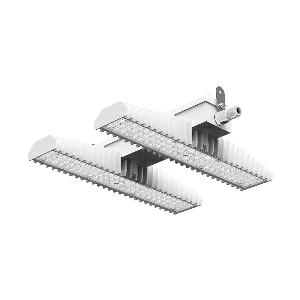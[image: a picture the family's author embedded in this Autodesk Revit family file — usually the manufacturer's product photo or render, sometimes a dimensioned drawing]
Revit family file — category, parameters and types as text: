
# Revit family: 3f_filippi_-_3f_lem_medio_3f_filippi_-_58911_-_3f_lem_2_led_100_dali_cr_medio
name_source: partatom
category: Lighting Fixtures
units: mm (PartAtom-declared; Revit-internal decimal feet)

## family parameters
Cut with Voids When Loaded = No
Host = Face
Light Source = No
Part Type = Normal
Room Calculation Point = No
Round Connector Dimension = Use Diameter
Shared = No

## types (1)
- 3F Filippi - 3F LEM Medio (1 x LED, 16630 lm, 109 W, 4000 K)
    Apparent Load = 109 VA
    Approval mark = CE
    CIE Flux Codes = 83 96 99 100 100
    Color Rendering = 80
    Color Temperature = 4000 K
    Control Gear = Electronic transformer
    Default Elevation = 1800 mm
    Description = Industrial luminaire with high light output and high luminous efficiency designed with the most innovative technologies for environments with temperature up to 55°C.

ILLUMINOTECHNICAL
Luminous efficiency 100% (DLOR 100%, ULOR 0%).
Initial luminous flux of the luminaire 16630 lm.
Medium distribution with rectangular shape.
Installation Interdistance Transv.D = 1.17 x hu - Long.D = 1.21 x hu.
Tabular UGR (CIE 117 - 4H-8H; S=0.25H; 70/50/20): RUG 18.5 - 18.1.
Beam angle: 65° - 67°.
Luminous efficacy 153 lm/W.
Lifetime (L93/B10): 30000 h. (tq+25°C)
Lifetime (L90/B10): 50000 h. (tq+25°C)
Lifetime (L85/B10): 80000 h. (tq+25°C)
Lifetime (L80/B10): 100000 h. (tq+25°C)
Lifetime (L85/B10): 50000 h. (tq+55°C)
Sudden decreased luminous flux after 50000 hours: 0% (C0).
Photobiological safety in compliance with IEC/TR 62778: RG0 risk exempt, (IEC 62471).
In compliance with IEC/EN 62722-2-1 - IEC/EN 62717 standards.

SOURCE
2 Mid-Power linear LED modules 50W/840.
Energy efficiency class (UE 2019/2020 - UE 2019/2015): C.
CIE 13.3 Colour rendering index: CRI >80 (R9 <50%).
IES TM-30 Fidelity Index: Rf = 84 Rg = 95.
CCT nominal colour temperature 4000 K.
Colour initial tolerance (MacAdam): SDCM 3.

MECHANICAL
Passive modular heatsinks in die-casted aluminium, painted in white colour.
To optimize the thermal management of the LED module, the heatsinks are oversized and provided with self-cleaning of cooling fins.
Wiring body in aluminium and galvanised steel anchored solidly to the sinks and thermally separated.
3F Lens lenses with high luminous efficiency, transparent methacrylate (PMMA), fixed to the LED modules.
Fixing brackets in stainless steel.
Luminaire with limited surface temperature. - D - (EN 60598-2-24)
Dimensions: 470x542 mm, height 129 mm. Weight 9.16 kg.
IP65 protection degree.
Mechanical strength to impacts IK06 (1 joule).
Glow-wire test resistance 650°C.

ELECTRICAL
Halogen Free DALI-2 DATI (Parts 251, 252, 253), PUSH-DIM, electronic wiring 230V-50/60Hz, power factor 0.97 at full load, THD <25%, constant output current, class I, 1 driver, 1 DALI addresse.
Power of the luminaire 109 W.
ENEC - CE.
Flicker: <4%.
Luminaire compliant with EN 60598-2-22 for power supply from a centralised emergency system CPSS (Central Power Supply System), not incorporated in the luminaire - high risk areas excluded. The default power and flux are 100% in AC and 15% in DC.
Ambient temperature from -30°C to +55°C.
Temperature class T6 max 85°C.
Quick connection via M25 5P connector with 9-13 mm tightening range.
Power unit positioned on a separate compartment by the LED module to ensure optimum temperatures of cabling components, to be inspectable and maintainable.
Relative humidity UR: <85%.

INSTALLATION
Ceiling / Suspended / Wall.
All accessories dedicated to this product are available on the Catalog and on our website www.3F-Filippi.com.

APPLICATIONS
In commercial environments, exhibition and industrial areas, stores, open areas.
Applications with high ambient temperature up to 55°C.
Environments in which it is necessary a total protection against falling fragments (eg environments with foodstuffs or machines with moving parts or with extreme temperature changes), use luminaires with polycarbonate lenses.

LIGHT MANAGEMENT
Recommended minimum setting: 10%.
The luminaire, equipped with (DALI-2 DATI) driver, can be controlled manually with 3F Easy Dim technology or automatically/manually with wired or wireless DALI/D2D control systems.
The D2D driver guarantees interoperability with other devices with the same certification by making the following information available:
Device Data (Part 251), Energy Report (Part 252), Diagnosis & Maintenance (Part 253).
In electrical systems without a regulation system (manual or automatic) and DALI bus, a suitable jumper must be made on the DA-DA terminals of the appliance.

WARNING
Fixture not suitable for cold stores with an ambient temperature <0°C and/or relative humidity >85%.
Luminaire designed for disposal/recycling at end-of-life.
Replaceable (LED only) light source by a professional. Replaceable control gear by a professional.
    Height = 129 mm
    Lamp = 1 x LED
    Lamp Light Flux = 16630 lm
    Lamp Power = 109 W
    Lamp count = 1
    Length = 470 mm
    Lifetime = 50000 h
    Luminous efficacy = 153 lm/W
    Manufacturer = 3F Filippi
    ModVariant = No
    Model = 3F Filippi - 58911 - 3F LEM 2 LED 100 DALI CR MEDIO
    Mounting Place = Ceiling
    Mounting Type = Pendant
    Number of Poles = 1
    OnlyDefault = Yes
    Power Factor = 1
    Product Name = 3F Filippi - 3F LEM Medio
    Product group = pendant luminaire
    ProductGroupID = 9
    Protection Class = Protection class I
    Protection Degree = IP 65
    RLX_Detail_Level = 1
    RLX_Emergency_Light_Flux = 0 lm
    RLX_Emergency_Type = 0
    RLX_Emergency_Type_DB = No
    RlxData = <blob elided: 98233 chars, md5=2e1ac0e3>
    Socket = socket
    Standby Power = 0 W
    System Light Flux = 16630 lm
    System Power = 109 W
    Type Comments = Product without accessories
    Type Image = 3f_filippi_-_lem_2.jpg
    URL = http://relux.com
    VarID = ---
    Voltage = 0 V
    Weight = 0.00 kg
    Width = 542 mm

## geometry (parser evidence)
native form markers: Blend x4, Sweep x12
no freeform markers — native parametric forms only
